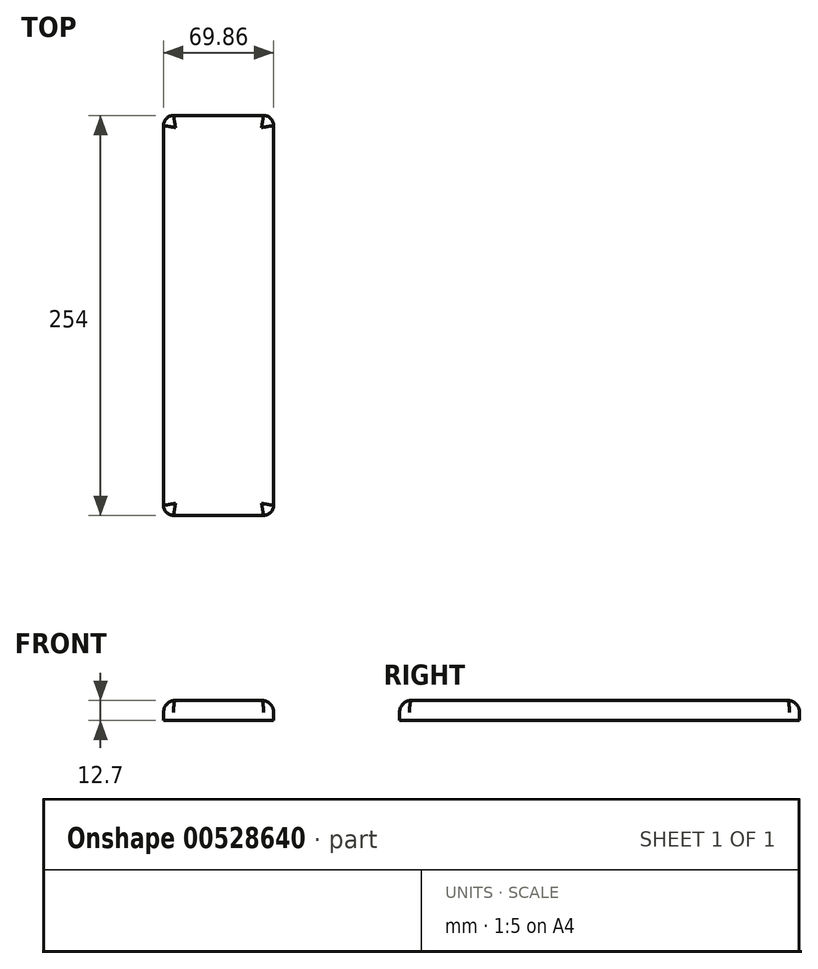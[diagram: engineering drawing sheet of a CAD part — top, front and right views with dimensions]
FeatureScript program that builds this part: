
annotation { "Feature Type Name" : "Feature", "Feature Type Description" : "" }
export const myFeature = defineFeature(function(context is Context, id is Id, definition is map)
    precondition{}
    {
        {
            var Q0;
            Q0=qCreatedBy(makeId("Top.planeOp"),FACE);
            var sketch = newSketch(context, id + "F0", { "sketchPlane" : qUnion([Q0])});
            skLineSegment(sketch, "E0.bottom", {"start": v(28.58, 127) * mm, "end": v(-28.57, 127) * mm});
            skLineSegment(sketch, "E0.top", {"start": v(28.57, -127) * mm, "end": v(-28.58, -127) * mm});
            skLineSegment(sketch, "E0.left", {"start": v(34.93, 120.65) * mm, "end": v(34.92, -120.65) * mm});
            skLineSegment(sketch, "E0.right", {"start": v(-34.92, 120.65) * mm, "end": v(-34.93, -120.65) * mm});
            skPoint(sketch, "E0.middle", {"position": v(0, 0) * mm});
            skPoint(sketch, "E1.visualSharp", {"position": v(-34.92, 127) * mm});
            skArc(sketch, "E1.filletArc", {"start": v(-28.57, 127) * mm, "mid": v(-33.07, 125.14) * mm, "end": v(-34.92, 120.65) * mm});
            skPoint(sketch, "E2.visualSharp", {"position": v(34.93, 127) * mm});
            skArc(sketch, "E2.filletArc", {"start": v(34.92, 120.65) * mm, "mid": v(33.07, 125.14) * mm, "end": v(28.58, 127) * mm});
            skPoint(sketch, "E3.visualSharp", {"position": v(-34.93, -127) * mm});
            skArc(sketch, "E3.filletArc", {"start": v(-34.93, -120.65) * mm, "mid": v(-33.07, -125.14) * mm, "end": v(-28.58, -127) * mm});
            skPoint(sketch, "E4.visualSharp", {"position": v(34.92, -127) * mm});
            skArc(sketch, "E4.filletArc", {"start": v(28.57, -127) * mm, "mid": v(33.07, -125.14) * mm, "end": v(34.92, -120.65) * mm});
            skSolve(sketch);
        }
        {
            var Q0;
            Q0 = qSketchRegion(id + "F0", true);
            extrude(context, id + "F1", {"entities" : qUnion([Q0]), "depth" : 12.7 * mm, "offsetDistance" : 25.4 * mm});
        }
        {
            var Q0;
            Q0=makeQuery(id+"F1.opExtrude","SWEPT_EDGE",EDGE,{"disambiguationData":[OSD([sQuery(id+"F0.wireOp",EDGE,"E0.top"),sQuery(id+"F0.wireOp",EDGE,"E0.left")])]});
            var Q1;
            Q1=makeQuery(id+"F1.opExtrude","SWEPT_EDGE",EDGE,{"disambiguationData":[OSD([sQuery(id+"F0.wireOp",EDGE,"E0.top"),sQuery(id+"F0.wireOp",EDGE,"E0.right")])]});
            var Q2;
            Q2=makeQuery(id+"F1.opExtrude","SWEPT_EDGE",EDGE,{"disambiguationData":[OSD([sQuery(id+"F0.wireOp",EDGE,"E0.bottom"),sQuery(id+"F0.wireOp",EDGE,"E0.left")])]});
            var Q3;
            Q3=makeQuery(id+"F1.opExtrude","SWEPT_EDGE",EDGE,{"disambiguationData":[OSD([sQuery(id+"F0.wireOp",EDGE,"E0.bottom"),sQuery(id+"F0.wireOp",EDGE,"E0.right")])]});
            var Q4;
            Q4=makeQuery(id+"F1.opExtrude","CAP_EDGE",EDGE,{"disambiguationData":[OSD([sQuery(id+"F0.wireOp",EDGE,"E0.bottom")])],"isStart":false});
            var Q5;
            Q5=makeQuery(id+"F1.opExtrude","CAP_EDGE",EDGE,{"disambiguationData":[OSD([sQuery(id+"F0.wireOp",EDGE,"E0.left")])],"isStart":false});
            var Q6;
            Q6=makeQuery(id+"F1.opExtrude","CAP_EDGE",EDGE,{"disambiguationData":[OSD([sQuery(id+"F0.wireOp",EDGE,"E0.right")])],"isStart":false});
            var Q7;
            Q7=makeQuery(id+"F1.opExtrude","CAP_EDGE",EDGE,{"disambiguationData":[OSD([sQuery(id+"F0.wireOp",EDGE,"E0.top")])],"isStart":false});
            fillet(context, id + "F2", {"entities" : qUnion([Q0, Q1, Q2, Q3, Q4, Q5, Q6, Q7]), "radius" : 7.62 * mm, "tangentPropagation" : true, "allowEdgeOverflow" : false});
        }
    });
